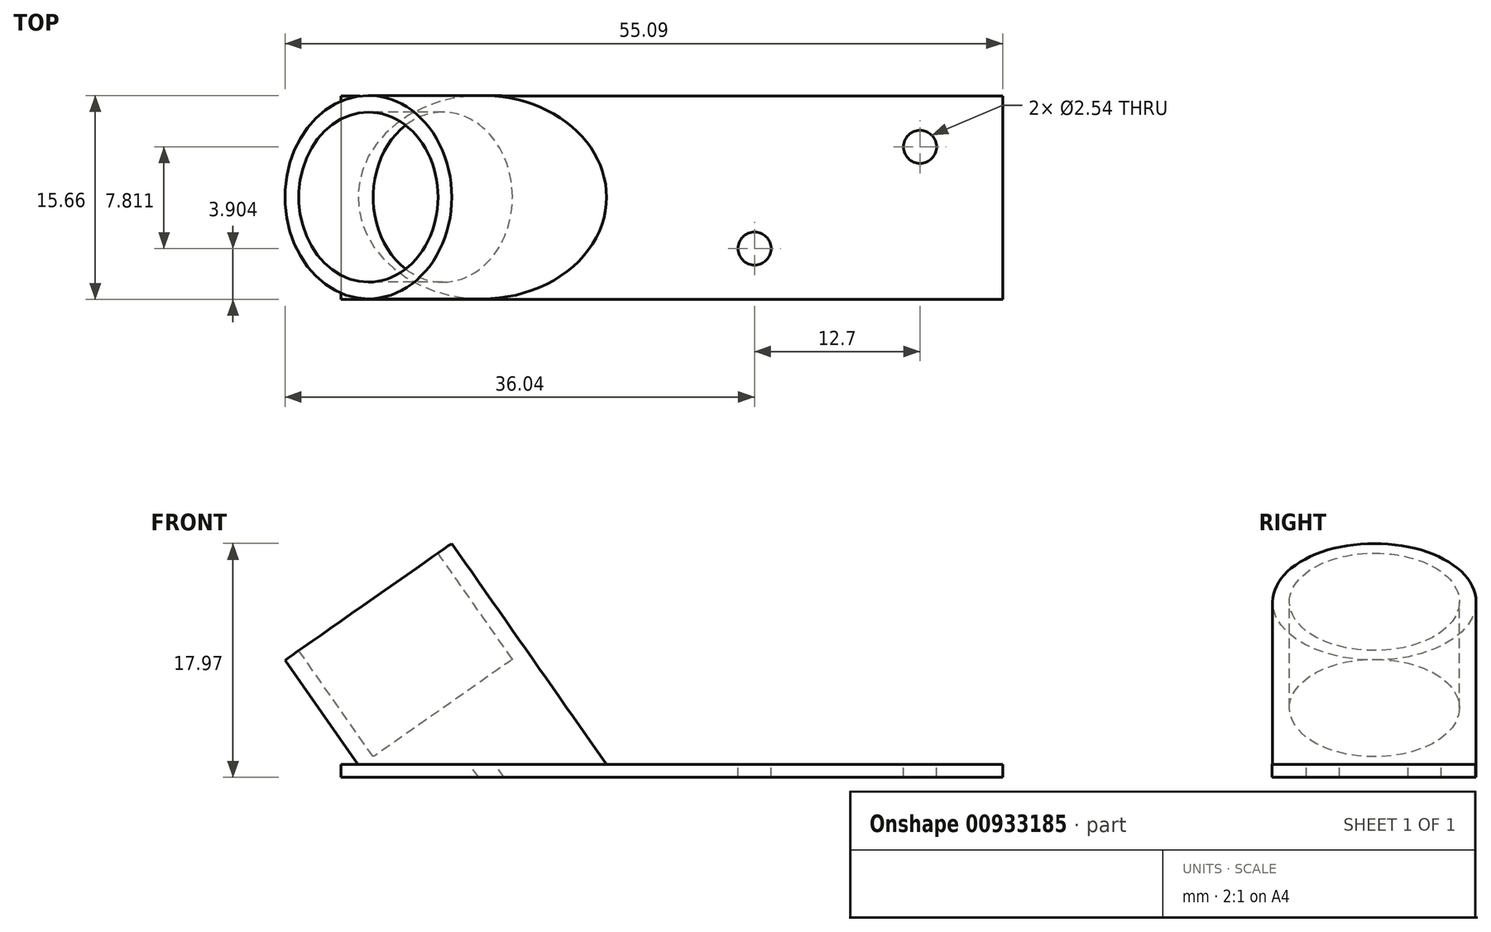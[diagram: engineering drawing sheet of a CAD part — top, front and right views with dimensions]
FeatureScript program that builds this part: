
annotation { "Feature Type Name" : "Feature", "Feature Type Description" : "" }
export const myFeature = defineFeature(function(context is Context, id is Id, definition is map)
    precondition{}
    {
        {
            var Q0;
            Q0=qCreatedBy(makeId("Top.planeOp"),FACE);
            var sketch = newSketch(context, id + "F0", { "sketchPlane" : qUnion([Q0])});
            skLineSegment(sketch, "E0.bottom", {"start": v(0, 0) * mm, "end": v(50.8, 0) * mm});
            skLineSegment(sketch, "E0.top", {"start": v(0, -15.62) * mm, "end": v(50.8, -15.62) * mm});
            skLineSegment(sketch, "E0.left", {"start": v(0, 0) * mm, "end": v(0, -15.62) * mm});
            skLineSegment(sketch, "E0.right", {"start": v(50.8, 0) * mm, "end": v(50.8, -15.62) * mm});
            skSolve(sketch);
        }
        {
            var Q0;
            Q0 = qSketchRegion(id + "F0", true);
            extrude(context, id + "F1", {"entities" : qUnion([Q0]), "depth" : 1 * mm, "offsetDistance" : 25.4 * mm});
        }
        {
            var Q0;
            Q0=makeQuery(id+"F1.opExtrude","CAP_EDGE",EDGE,{"disambiguationData":[OSD([sQuery(id+"F0.wireOp",EDGE,"E0.left")])],"isStart":false});
            var Q1;
            Q1=makeQuery(id+"F1.opExtrude","CAP_FACE",FACE,{"disambiguationData":[OSD([sQuery(id+"F0.wireOp",EDGE,"E0.bottom"),sQuery(id+"F0.wireOp",EDGE,"E0.top"),sQuery(id+"F0.wireOp",EDGE,"E0.left"),sQuery(id+"F0.wireOp",EDGE,"E0.right")])],"isStart":false});
            cPlane(context, id + "F2", {"entities" : qUnion([Q0, Q1]), "cplaneType" : CPlaneType.LINE_ANGLE, "offset" : 25.4 * mm, "angle" : 215 * degree, "width" : 152.4 * mm, "height" : 152.4 * mm});
        }
        {
            var Q0;
            Q0=qCreatedBy(id+"F2.planeOp",FACE);
            var sketch = newSketch(context, id + "F3", { "sketchPlane" : qUnion([Q0])});
            skCircle(sketch, "E1", {"center": v(9.46, -7.77) * mm, "radius": 7.81 * mm});
            skSolve(sketch);
        }
        {
            var Q0;
            Q0=makeQuery(id+"F3.imprint","IMPRINT",FACE,{"disambiguationData":[TD([[makeQuery(id+"F3.imprint","IMPRINT",EDGE,{"derivedFrom":sQuery(id+"F3.wireOp",EDGE,"E1")}),1.0]])]});
            extrude(context, id + "F4", {"entities" : qUnion([Q0]), "operationType" : NewBodyOperationType.ADD, "oppositeDirection" : true, "depth" : 14.5 * mm, "offsetDistance" : 25.4 * mm, "hasSecondDirection" : true, "secondDirectionOppositeDirection" : false, "secondDirectionDepth" : 9.02 * mm});
        }
        {
            var Q0;
            Q0=makeQuery(id+"F1.opExtrude","CAP_FACE",FACE,{"disambiguationData":[OSD([sQuery(id+"F0.wireOp",EDGE,"E0.bottom"),sQuery(id+"F0.wireOp",EDGE,"E0.top"),sQuery(id+"F0.wireOp",EDGE,"E0.left"),sQuery(id+"F0.wireOp",EDGE,"E0.right")])],"isStart":true});
            var sketch = newSketch(context, id + "F5", { "sketchPlane" : qUnion([Q0])});
            skSolve(sketch);
        }
        {
            var Q0;
            {var subQ3=sQuery(id+"F0.wireOp",EDGE,"E0.top");Q0=makeQuery(id+"F5.imprint","IMPRINT",FACE,{"disambiguationData":[TD([[makeQuery(id+"F5.imprint","IMPRINT",EDGE,{"derivedFrom":makeQuery(id+"F1.opExtrude","CAP_EDGE",EDGE,{"disambiguationData":[OSD([subQ3])],"isStart":true})}),-1.0]])]});}
            var sketch = newSketch(context, id + "F6", { "sketchPlane" : qUnion([Q0])});
            skLineSegment(sketch, "E2.bottom", {"start": v(-18.49, 30.8) * mm, "end": v(41.43, 30.8) * mm});
            skLineSegment(sketch, "E2.top", {"start": v(-18.49, -14.22) * mm, "end": v(41.43, -14.22) * mm});
            skLineSegment(sketch, "E2.left", {"start": v(-18.49, 30.8) * mm, "end": v(-18.49, -14.22) * mm});
            skLineSegment(sketch, "E2.right", {"start": v(41.43, 30.8) * mm, "end": v(41.43, -14.22) * mm});
            skSolve(sketch);
        }
        {
            var Q0;
            Q0 = qSketchRegion(id + "F6", true);
            extrude(context, id + "F7", {"entities" : qUnion([Q0]), "operationType" : NewBodyOperationType.REMOVE, "depth" : 25.15 * mm, "offsetDistance" : 25.4 * mm});
        }
        {
            var Q0;
            Q0=makeQuery(id+"F4.opExtrude","CAP_FACE",FACE,{"disambiguationData":[OSD([sQuery(id+"F3.wireOp",EDGE,"E1")])],"isStart":true});
            var sketch = newSketch(context, id + "F8", { "sketchPlane" : qUnion([Q0])});
            skCircle(sketch, "E3", {"center": v(9.46, -7.77) * mm, "radius": 6.52 * mm});
            skSolve(sketch);
        }
        {
            var Q0;
            Q0 = qSketchRegion(id + "F8", true);
            extrude(context, id + "F9", {"entities" : qUnion([Q0]), "operationType" : NewBodyOperationType.REMOVE, "oppositeDirection" : true, "depth" : 9.96 * mm, "offsetDistance" : 25.4 * mm});
        }
        {
            var Q0;
            Q0=makeQuery(id+"F1.opExtrude","CAP_FACE",FACE,{"disambiguationData":[OSD([sQuery(id+"F0.wireOp",EDGE,"E0.bottom"),sQuery(id+"F0.wireOp",EDGE,"E0.top"),sQuery(id+"F0.wireOp",EDGE,"E0.left"),sQuery(id+"F0.wireOp",EDGE,"E0.right")])],"isStart":false});
            var sketch = newSketch(context, id + "F10", { "sketchPlane" : qUnion([Q0])});
            skLineSegment(sketch, "E4", {"start": v(25.4, -15.62) * mm, "end": v(25.4, 0) * mm, "construction": true});
            skLineSegment(sketch, "E5", {"start": v(25.4, 0) * mm, "end": v(50.8, -15.62) * mm, "construction": true});
            skLineSegment(sketch, "E6", {"start": v(50.8, -15.62) * mm, "end": v(50.8, 0) * mm, "construction": true});
            skLineSegment(sketch, "E7", {"start": v(50.8, 0) * mm, "end": v(25.4, -15.62) * mm, "construction": true});
            skLineSegment(sketch, "E8", {"start": v(38.1, -7.81) * mm, "end": v(25.4, -7.81) * mm, "construction": true});
            skLineSegment(sketch, "E9", {"start": v(25.4, -7.81) * mm, "end": v(38.1, -15.62) * mm, "construction": true});
            skLineSegment(sketch, "E10", {"start": v(38.1, -15.62) * mm, "end": v(38.1, 0) * mm, "construction": true});
            skLineSegment(sketch, "E11", {"start": v(38.1, 0) * mm, "end": v(50.8, -7.81) * mm, "construction": true});
            skLineSegment(sketch, "E12", {"start": v(38.1, -7.81) * mm, "end": v(50.8, -7.81) * mm, "construction": true});
            skCircle(sketch, "E13", {"center": v(31.75, -11.72) * mm, "radius": 1.27 * mm});
            skCircle(sketch, "E14", {"center": v(44.45, -3.9) * mm, "radius": 1.27 * mm});
            skSolve(sketch);
        }
        {
            var Q0;
            Q0 = qSketchRegion(id + "F10", true);
            extrude(context, id + "F11", {"entities" : qUnion([Q0]), "operationType" : NewBodyOperationType.REMOVE, "oppositeDirection" : true, "depth" : 91.64 * mm, "offsetDistance" : 25.4 * mm});
        }
    });
